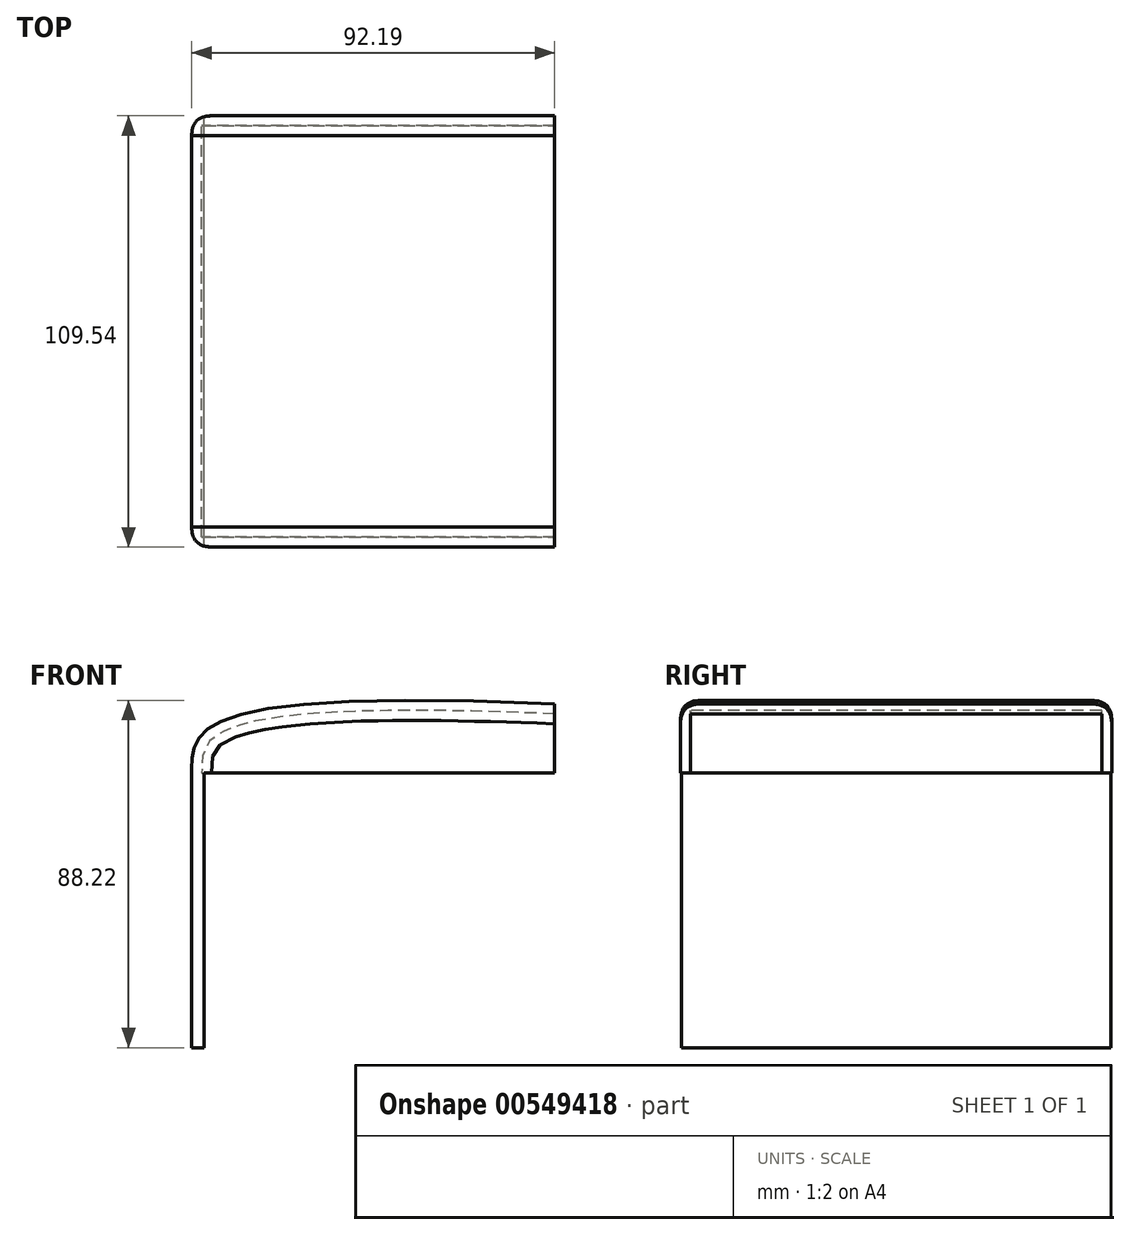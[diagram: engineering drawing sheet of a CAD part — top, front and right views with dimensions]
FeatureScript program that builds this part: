
annotation { "Feature Type Name" : "Feature", "Feature Type Description" : "" }
export const myFeature = defineFeature(function(context is Context, id is Id, definition is map)
    precondition{}
    {
        {
            var Q0;
            Q0=qCreatedBy(makeId("Front.planeOp"),FACE);
            var sketch = newSketch(context, id + "F0", { "sketchPlane" : qUnion([Q0])});
            skFitSpline(sketch, "E0", {"points": [v(92.2, 17.5) * mm, v(0, 0) * mm, v(0, -69.85) * mm], "startDerivative": vector(-515.21, 21.78) * mm, "endDerivative": vector(0, -313.87) * mm});
            skLineSegment(sketch, "E1", {"start": v(0, -69.85) * mm, "end": v(3.18, -69.85) * mm});
            skLineSegment(sketch, "E2", {"start": v(92.2, 17.5) * mm, "end": v(92.2, 14.32) * mm});
            skLineSegment(sketch, "E3", {"start": v(3.18, -69.85) * mm, "end": v(3.18, 0) * mm});
            skFitSpline(sketch, "E4", {"points": [v(3.17, 0) * mm, v(92.2, 14.32) * mm], "startDerivative": vector(30.34, 64.93) * mm, "endDerivative": vector(123.16, 4.52) * mm});
            skLineSegment(sketch, "E5", {"start": v(3.17, 0) * mm, "end": v(92.2, 0) * mm});
            skLineSegment(sketch, "E6", {"start": v(92.2, 0) * mm, "end": v(92.2, 14.32) * mm});
            skSolve(sketch);
        }
        {
            var Q0;
            Q0=makeQuery(id+"F0.imprint","IMPRINT",FACE,{"disambiguationData":[TD([[makeQuery(id+"F0.imprint","IMPRINT",EDGE,{"derivedFrom":sQuery(id+"F0.wireOp",EDGE,"E0")}),1.0]])]});
            extrude(context, id + "F1", {"entities" : qUnion([Q0]), "endBound" : BoundingType.SYMMETRIC, "depth" : 109.54 * mm, "offsetDistance" : 25.4 * mm});
        }
        {
            var Q0;
            Q0 = qSketchRegion(id + "F0", true);
            extrude(context, id + "F2", {"entities" : qUnion([Q0]), "operationType" : NewBodyOperationType.ADD, "endBound" : BoundingType.SYMMETRIC, "depth" : 109.54 * mm, "offsetDistance" : 25.4 * mm});
        }
        {
            var Q0;
            {var subQ0=sQuery(id+"F0.wireOp",EDGE,"E2");Q0=makeQuery(id+"F2.boolean.opBoolean","MERGE",FACE,{"derivedFrom":[makeQuery(id+"F1.opExtrude","SWEPT_FACE",FACE,{"disambiguationData":[OSD([subQ0])]}),makeQuery(id+"F2.opExtrude","SWEPT_FACE",FACE,{"disambiguationData":[OSD([subQ0,sQuery(id+"F0.wireOp",EDGE,"E6")])]})]});}
            var Q1;
            Q1=makeQuery(id+"F2.opExtrude","SWEPT_FACE",FACE,{"disambiguationData":[OSD([sQuery(id+"F0.wireOp",EDGE,"E5")])]});
            shell(context, id + "F3", {"entities" : qUnion([Q0, Q1]), "thickness" : 2.54 * mm});
        }
        {
            var Q0;
            Q0=makeQuery(id+"F1.opExtrude","CAP_EDGE",EDGE,{"disambiguationData":[OSD([sQuery(id+"F0.wireOp",EDGE,"E0")])],"isStart":false});
            fillet(context, id + "F4", {"entities" : qUnion([Q0]), "radius" : 5.08 * mm, "tangentPropagation" : true, "rho" : 0.5, "crossSection" : FilletCrossSection.CONIC, "allowEdgeOverflow" : false});
        }
        {
            var Q0;
            Q0=makeQuery(id+"F1.opExtrude","CAP_EDGE",EDGE,{"disambiguationData":[OSD([sQuery(id+"F0.wireOp",EDGE,"E0")])],"isStart":true});
            fillet(context, id + "F5", {"entities" : qUnion([Q0]), "radius" : 5.08 * mm, "tangentPropagation" : true, "rho" : 0.5, "crossSection" : FilletCrossSection.CONIC, "allowEdgeOverflow" : false});
        }
    });
